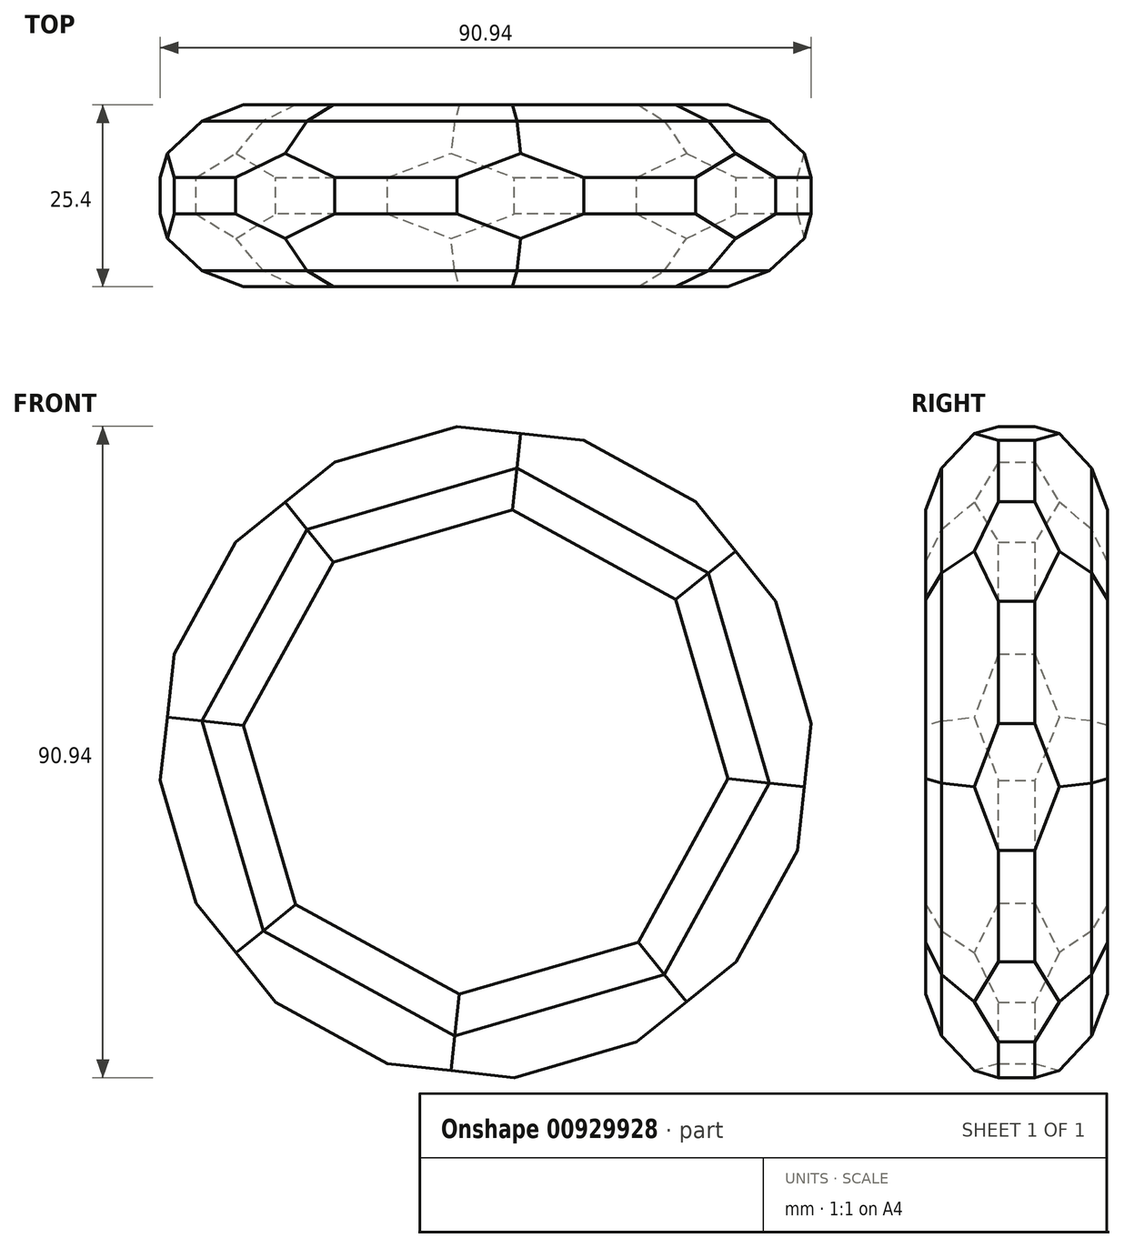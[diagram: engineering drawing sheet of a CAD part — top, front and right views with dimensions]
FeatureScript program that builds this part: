
annotation { "Feature Type Name" : "Feature", "Feature Type Description" : "" }
export const myFeature = defineFeature(function(context is Context, id is Id, definition is map)
    precondition{}
    {
        {
            var Q0;
            Q0=qCreatedBy(makeId("Front.planeOp"),FACE);
            var sketch = newSketch(context, id + "F0", { "sketchPlane" : qUnion([Q0])});
            skCircle(sketch, "E0.cCircle", {"center": v(0, 0) * mm, "radius": 44.76 * mm, "construction": true});
            skLineSegment(sketch, "E0.0", {"start": v(29.33, 34.97) * mm, "end": v(40.48, 21.08) * mm});
            skLineSegment(sketch, "E0.1", {"start": v(40.48, 21.08) * mm, "end": v(45.47, 3.99) * mm});
            skLineSegment(sketch, "E0.2", {"start": v(45.47, 3.99) * mm, "end": v(43.53, -13.72) * mm});
            skLineSegment(sketch, "E0.3", {"start": v(43.53, -13.72) * mm, "end": v(34.97, -29.33) * mm});
            skLineSegment(sketch, "E0.4", {"start": v(34.97, -29.33) * mm, "end": v(21.08, -40.48) * mm});
            skLineSegment(sketch, "E0.5", {"start": v(21.08, -40.48) * mm, "end": v(3.99, -45.47) * mm});
            skLineSegment(sketch, "E0.6", {"start": v(3.99, -45.47) * mm, "end": v(-13.72, -43.53) * mm});
            skLineSegment(sketch, "E0.7", {"start": v(-13.72, -43.53) * mm, "end": v(-29.33, -34.97) * mm});
            skLineSegment(sketch, "E0.8", {"start": v(-29.33, -34.97) * mm, "end": v(-40.48, -21.08) * mm});
            skLineSegment(sketch, "E0.9", {"start": v(-40.48, -21.08) * mm, "end": v(-45.47, -3.99) * mm});
            skLineSegment(sketch, "E0.10", {"start": v(-45.47, -3.99) * mm, "end": v(-43.53, 13.72) * mm});
            skLineSegment(sketch, "E0.11", {"start": v(-43.53, 13.72) * mm, "end": v(-34.97, 29.33) * mm});
            skLineSegment(sketch, "E0.12", {"start": v(-34.97, 29.33) * mm, "end": v(-21.08, 40.48) * mm});
            skLineSegment(sketch, "E0.13", {"start": v(-21.08, 40.48) * mm, "end": v(-3.99, 45.47) * mm});
            skLineSegment(sketch, "E0.14", {"start": v(-3.99, 45.47) * mm, "end": v(13.72, 43.53) * mm});
            skLineSegment(sketch, "E0.15", {"start": v(13.72, 43.53) * mm, "end": v(29.33, 34.97) * mm});
            skPoint(sketch, "E0.0.midPoint", {"position": v(34.9, 28.03) * mm});
            skSolve(sketch);
        }
        {
            var Q0;
            Q0 = qSketchRegion(id + "F0", true);
            extrude(context, id + "F1", {"entities" : qUnion([Q0]), "depth" : 25.4 * mm, "offsetDistance" : 25.4 * mm});
        }
        {
            var Q0;
            Q0=makeQuery(id+"F1.opExtrude","CAP_EDGE",EDGE,{"disambiguationData":[OSD([sQuery(id+"F0.wireOp",EDGE,"E0.3")])],"isStart":false});
            var Q1;
            Q1=makeQuery(id+"F1.opExtrude","CAP_EDGE",EDGE,{"disambiguationData":[OSD([sQuery(id+"F0.wireOp",EDGE,"E0.1")])],"isStart":false});
            var Q2;
            Q2=makeQuery(id+"F1.opExtrude","CAP_EDGE",EDGE,{"disambiguationData":[OSD([sQuery(id+"F0.wireOp",EDGE,"E0.15")])],"isStart":false});
            var Q3;
            Q3=makeQuery(id+"F1.opExtrude","CAP_EDGE",EDGE,{"disambiguationData":[OSD([sQuery(id+"F0.wireOp",EDGE,"E0.13")])],"isStart":false});
            var Q4;
            Q4=makeQuery(id+"F1.opExtrude","CAP_EDGE",EDGE,{"disambiguationData":[OSD([sQuery(id+"F0.wireOp",EDGE,"E0.11")])],"isStart":false});
            var Q5;
            Q5=makeQuery(id+"F1.opExtrude","CAP_EDGE",EDGE,{"disambiguationData":[OSD([sQuery(id+"F0.wireOp",EDGE,"E0.9")])],"isStart":false});
            var Q6;
            Q6=makeQuery(id+"F1.opExtrude","CAP_EDGE",EDGE,{"disambiguationData":[OSD([sQuery(id+"F0.wireOp",EDGE,"E0.7")])],"isStart":false});
            var Q7;
            Q7=makeQuery(id+"F1.opExtrude","CAP_EDGE",EDGE,{"disambiguationData":[OSD([sQuery(id+"F0.wireOp",EDGE,"E0.5")])],"isStart":false});
            chamfer(context, id + "F2", {"entities" : qUnion([Q0, Q1, Q2, Q3, Q4, Q5, Q6, Q7]), "width" : 10.16 * mm, "tangentPropagation" : true});
        }
        {
            var Q0;
            {var subQ0=sQuery(id+"F0.wireOp",EDGE,"E0.11");Q0=makeQuery(id+"F2.opChamfer","BLEND_EDGE",EDGE,{"blendedFrom":[makeQuery(id+"F1.opExtrude","CAP_EDGE",EDGE,{"disambiguationData":[OSD([subQ0])],"isStart":false}),makeQuery(id+"F1.opExtrude","CAP_FACE",FACE,{"disambiguationData":[OSD([sQuery(id+"F0.wireOp",EDGE,"E0.0"),sQuery(id+"F0.wireOp",EDGE,"E0.1"),sQuery(id+"F0.wireOp",EDGE,"E0.2"),sQuery(id+"F0.wireOp",EDGE,"E0.3"),sQuery(id+"F0.wireOp",EDGE,"E0.4"),sQuery(id+"F0.wireOp",EDGE,"E0.5"),sQuery(id+"F0.wireOp",EDGE,"E0.6"),sQuery(id+"F0.wireOp",EDGE,"E0.7"),sQuery(id+"F0.wireOp",EDGE,"E0.8"),sQuery(id+"F0.wireOp",EDGE,"E0.9"),sQuery(id+"F0.wireOp",EDGE,"E0.10"),subQ0,sQuery(id+"F0.wireOp",EDGE,"E0.12"),sQuery(id+"F0.wireOp",EDGE,"E0.13"),sQuery(id+"F0.wireOp",EDGE,"E0.14"),sQuery(id+"F0.wireOp",EDGE,"E0.15")])],"isStart":false})],"blendedInto":[makeQuery(id+"F1.opExtrude","CAP_FACE",FACE,{"disambiguationData":[OSD([sQuery(id+"F0.wireOp",EDGE,"E0.0"),sQuery(id+"F0.wireOp",EDGE,"E0.1"),sQuery(id+"F0.wireOp",EDGE,"E0.2"),sQuery(id+"F0.wireOp",EDGE,"E0.3"),sQuery(id+"F0.wireOp",EDGE,"E0.4"),sQuery(id+"F0.wireOp",EDGE,"E0.5"),sQuery(id+"F0.wireOp",EDGE,"E0.6"),sQuery(id+"F0.wireOp",EDGE,"E0.7"),sQuery(id+"F0.wireOp",EDGE,"E0.8"),sQuery(id+"F0.wireOp",EDGE,"E0.9"),sQuery(id+"F0.wireOp",EDGE,"E0.10"),subQ0,sQuery(id+"F0.wireOp",EDGE,"E0.12"),sQuery(id+"F0.wireOp",EDGE,"E0.13"),sQuery(id+"F0.wireOp",EDGE,"E0.14"),sQuery(id+"F0.wireOp",EDGE,"E0.15")])],"isStart":false})]});}
            var Q1;
            {var subQ0=sQuery(id+"F0.wireOp",EDGE,"E0.15");Q1=makeQuery(id+"F2.opChamfer","BLEND_EDGE",EDGE,{"blendedFrom":[makeQuery(id+"F1.opExtrude","CAP_EDGE",EDGE,{"disambiguationData":[OSD([subQ0])],"isStart":false}),makeQuery(id+"F1.opExtrude","CAP_FACE",FACE,{"disambiguationData":[OSD([sQuery(id+"F0.wireOp",EDGE,"E0.0"),sQuery(id+"F0.wireOp",EDGE,"E0.1"),sQuery(id+"F0.wireOp",EDGE,"E0.2"),sQuery(id+"F0.wireOp",EDGE,"E0.3"),sQuery(id+"F0.wireOp",EDGE,"E0.4"),sQuery(id+"F0.wireOp",EDGE,"E0.5"),sQuery(id+"F0.wireOp",EDGE,"E0.6"),sQuery(id+"F0.wireOp",EDGE,"E0.7"),sQuery(id+"F0.wireOp",EDGE,"E0.8"),sQuery(id+"F0.wireOp",EDGE,"E0.9"),sQuery(id+"F0.wireOp",EDGE,"E0.10"),sQuery(id+"F0.wireOp",EDGE,"E0.11"),sQuery(id+"F0.wireOp",EDGE,"E0.12"),sQuery(id+"F0.wireOp",EDGE,"E0.13"),sQuery(id+"F0.wireOp",EDGE,"E0.14"),subQ0])],"isStart":false})],"blendedInto":[makeQuery(id+"F1.opExtrude","CAP_FACE",FACE,{"disambiguationData":[OSD([sQuery(id+"F0.wireOp",EDGE,"E0.0"),sQuery(id+"F0.wireOp",EDGE,"E0.1"),sQuery(id+"F0.wireOp",EDGE,"E0.2"),sQuery(id+"F0.wireOp",EDGE,"E0.3"),sQuery(id+"F0.wireOp",EDGE,"E0.4"),sQuery(id+"F0.wireOp",EDGE,"E0.5"),sQuery(id+"F0.wireOp",EDGE,"E0.6"),sQuery(id+"F0.wireOp",EDGE,"E0.7"),sQuery(id+"F0.wireOp",EDGE,"E0.8"),sQuery(id+"F0.wireOp",EDGE,"E0.9"),sQuery(id+"F0.wireOp",EDGE,"E0.10"),sQuery(id+"F0.wireOp",EDGE,"E0.11"),sQuery(id+"F0.wireOp",EDGE,"E0.12"),sQuery(id+"F0.wireOp",EDGE,"E0.13"),sQuery(id+"F0.wireOp",EDGE,"E0.14"),subQ0])],"isStart":false})]});}
            var Q2;
            {var subQ0=sQuery(id+"F0.wireOp",EDGE,"E0.3");Q2=makeQuery(id+"F2.opChamfer","BLEND_EDGE",EDGE,{"blendedFrom":[makeQuery(id+"F1.opExtrude","CAP_EDGE",EDGE,{"disambiguationData":[OSD([subQ0])],"isStart":false}),makeQuery(id+"F1.opExtrude","CAP_FACE",FACE,{"disambiguationData":[OSD([sQuery(id+"F0.wireOp",EDGE,"E0.0"),sQuery(id+"F0.wireOp",EDGE,"E0.1"),sQuery(id+"F0.wireOp",EDGE,"E0.2"),subQ0,sQuery(id+"F0.wireOp",EDGE,"E0.4"),sQuery(id+"F0.wireOp",EDGE,"E0.5"),sQuery(id+"F0.wireOp",EDGE,"E0.6"),sQuery(id+"F0.wireOp",EDGE,"E0.7"),sQuery(id+"F0.wireOp",EDGE,"E0.8"),sQuery(id+"F0.wireOp",EDGE,"E0.9"),sQuery(id+"F0.wireOp",EDGE,"E0.10"),sQuery(id+"F0.wireOp",EDGE,"E0.11"),sQuery(id+"F0.wireOp",EDGE,"E0.12"),sQuery(id+"F0.wireOp",EDGE,"E0.13"),sQuery(id+"F0.wireOp",EDGE,"E0.14"),sQuery(id+"F0.wireOp",EDGE,"E0.15")])],"isStart":false})],"blendedInto":[makeQuery(id+"F1.opExtrude","CAP_FACE",FACE,{"disambiguationData":[OSD([sQuery(id+"F0.wireOp",EDGE,"E0.0"),sQuery(id+"F0.wireOp",EDGE,"E0.1"),sQuery(id+"F0.wireOp",EDGE,"E0.2"),subQ0,sQuery(id+"F0.wireOp",EDGE,"E0.4"),sQuery(id+"F0.wireOp",EDGE,"E0.5"),sQuery(id+"F0.wireOp",EDGE,"E0.6"),sQuery(id+"F0.wireOp",EDGE,"E0.7"),sQuery(id+"F0.wireOp",EDGE,"E0.8"),sQuery(id+"F0.wireOp",EDGE,"E0.9"),sQuery(id+"F0.wireOp",EDGE,"E0.10"),sQuery(id+"F0.wireOp",EDGE,"E0.11"),sQuery(id+"F0.wireOp",EDGE,"E0.12"),sQuery(id+"F0.wireOp",EDGE,"E0.13"),sQuery(id+"F0.wireOp",EDGE,"E0.14"),sQuery(id+"F0.wireOp",EDGE,"E0.15")])],"isStart":false})]});}
            var Q3;
            {var subQ0=sQuery(id+"F0.wireOp",EDGE,"E0.7");Q3=makeQuery(id+"F2.opChamfer","BLEND_EDGE",EDGE,{"blendedFrom":[makeQuery(id+"F1.opExtrude","CAP_EDGE",EDGE,{"disambiguationData":[OSD([subQ0])],"isStart":false}),makeQuery(id+"F1.opExtrude","CAP_FACE",FACE,{"disambiguationData":[OSD([sQuery(id+"F0.wireOp",EDGE,"E0.0"),sQuery(id+"F0.wireOp",EDGE,"E0.1"),sQuery(id+"F0.wireOp",EDGE,"E0.2"),sQuery(id+"F0.wireOp",EDGE,"E0.3"),sQuery(id+"F0.wireOp",EDGE,"E0.4"),sQuery(id+"F0.wireOp",EDGE,"E0.5"),sQuery(id+"F0.wireOp",EDGE,"E0.6"),subQ0,sQuery(id+"F0.wireOp",EDGE,"E0.8"),sQuery(id+"F0.wireOp",EDGE,"E0.9"),sQuery(id+"F0.wireOp",EDGE,"E0.10"),sQuery(id+"F0.wireOp",EDGE,"E0.11"),sQuery(id+"F0.wireOp",EDGE,"E0.12"),sQuery(id+"F0.wireOp",EDGE,"E0.13"),sQuery(id+"F0.wireOp",EDGE,"E0.14"),sQuery(id+"F0.wireOp",EDGE,"E0.15")])],"isStart":false})],"blendedInto":[makeQuery(id+"F1.opExtrude","CAP_FACE",FACE,{"disambiguationData":[OSD([sQuery(id+"F0.wireOp",EDGE,"E0.0"),sQuery(id+"F0.wireOp",EDGE,"E0.1"),sQuery(id+"F0.wireOp",EDGE,"E0.2"),sQuery(id+"F0.wireOp",EDGE,"E0.3"),sQuery(id+"F0.wireOp",EDGE,"E0.4"),sQuery(id+"F0.wireOp",EDGE,"E0.5"),sQuery(id+"F0.wireOp",EDGE,"E0.6"),subQ0,sQuery(id+"F0.wireOp",EDGE,"E0.8"),sQuery(id+"F0.wireOp",EDGE,"E0.9"),sQuery(id+"F0.wireOp",EDGE,"E0.10"),sQuery(id+"F0.wireOp",EDGE,"E0.11"),sQuery(id+"F0.wireOp",EDGE,"E0.12"),sQuery(id+"F0.wireOp",EDGE,"E0.13"),sQuery(id+"F0.wireOp",EDGE,"E0.14"),sQuery(id+"F0.wireOp",EDGE,"E0.15")])],"isStart":false})]});}
            chamfer(context, id + "F3", {"entities" : qUnion([Q0, Q1, Q2, Q3]), "width" : 7.62 * mm, "tangentPropagation" : true});
        }
        {
            var Q0;
            {var subQ0=sQuery(id+"F0.wireOp",EDGE,"E0.13");Q0=makeQuery(id+"F2.opChamfer","BLEND_EDGE",EDGE,{"blendedFrom":[makeQuery(id+"F1.opExtrude","CAP_EDGE",EDGE,{"disambiguationData":[OSD([subQ0])],"isStart":false}),makeQuery(id+"F1.opExtrude","CAP_FACE",FACE,{"disambiguationData":[OSD([sQuery(id+"F0.wireOp",EDGE,"E0.0"),sQuery(id+"F0.wireOp",EDGE,"E0.1"),sQuery(id+"F0.wireOp",EDGE,"E0.2"),sQuery(id+"F0.wireOp",EDGE,"E0.3"),sQuery(id+"F0.wireOp",EDGE,"E0.4"),sQuery(id+"F0.wireOp",EDGE,"E0.5"),sQuery(id+"F0.wireOp",EDGE,"E0.6"),sQuery(id+"F0.wireOp",EDGE,"E0.7"),sQuery(id+"F0.wireOp",EDGE,"E0.8"),sQuery(id+"F0.wireOp",EDGE,"E0.9"),sQuery(id+"F0.wireOp",EDGE,"E0.10"),sQuery(id+"F0.wireOp",EDGE,"E0.11"),sQuery(id+"F0.wireOp",EDGE,"E0.12"),subQ0,sQuery(id+"F0.wireOp",EDGE,"E0.14"),sQuery(id+"F0.wireOp",EDGE,"E0.15")])],"isStart":false})],"blendedInto":[makeQuery(id+"F1.opExtrude","CAP_FACE",FACE,{"disambiguationData":[OSD([sQuery(id+"F0.wireOp",EDGE,"E0.0"),sQuery(id+"F0.wireOp",EDGE,"E0.1"),sQuery(id+"F0.wireOp",EDGE,"E0.2"),sQuery(id+"F0.wireOp",EDGE,"E0.3"),sQuery(id+"F0.wireOp",EDGE,"E0.4"),sQuery(id+"F0.wireOp",EDGE,"E0.5"),sQuery(id+"F0.wireOp",EDGE,"E0.6"),sQuery(id+"F0.wireOp",EDGE,"E0.7"),sQuery(id+"F0.wireOp",EDGE,"E0.8"),sQuery(id+"F0.wireOp",EDGE,"E0.9"),sQuery(id+"F0.wireOp",EDGE,"E0.10"),sQuery(id+"F0.wireOp",EDGE,"E0.11"),sQuery(id+"F0.wireOp",EDGE,"E0.12"),subQ0,sQuery(id+"F0.wireOp",EDGE,"E0.14"),sQuery(id+"F0.wireOp",EDGE,"E0.15")])],"isStart":false})]});}
            var Q1;
            {var subQ0=sQuery(id+"F0.wireOp",EDGE,"E0.1");Q1=makeQuery(id+"F2.opChamfer","BLEND_EDGE",EDGE,{"blendedFrom":[makeQuery(id+"F1.opExtrude","CAP_EDGE",EDGE,{"disambiguationData":[OSD([subQ0])],"isStart":false}),makeQuery(id+"F1.opExtrude","CAP_FACE",FACE,{"disambiguationData":[OSD([sQuery(id+"F0.wireOp",EDGE,"E0.0"),subQ0,sQuery(id+"F0.wireOp",EDGE,"E0.2"),sQuery(id+"F0.wireOp",EDGE,"E0.3"),sQuery(id+"F0.wireOp",EDGE,"E0.4"),sQuery(id+"F0.wireOp",EDGE,"E0.5"),sQuery(id+"F0.wireOp",EDGE,"E0.6"),sQuery(id+"F0.wireOp",EDGE,"E0.7"),sQuery(id+"F0.wireOp",EDGE,"E0.8"),sQuery(id+"F0.wireOp",EDGE,"E0.9"),sQuery(id+"F0.wireOp",EDGE,"E0.10"),sQuery(id+"F0.wireOp",EDGE,"E0.11"),sQuery(id+"F0.wireOp",EDGE,"E0.12"),sQuery(id+"F0.wireOp",EDGE,"E0.13"),sQuery(id+"F0.wireOp",EDGE,"E0.14"),sQuery(id+"F0.wireOp",EDGE,"E0.15")])],"isStart":false})],"blendedInto":[makeQuery(id+"F1.opExtrude","CAP_FACE",FACE,{"disambiguationData":[OSD([sQuery(id+"F0.wireOp",EDGE,"E0.0"),subQ0,sQuery(id+"F0.wireOp",EDGE,"E0.2"),sQuery(id+"F0.wireOp",EDGE,"E0.3"),sQuery(id+"F0.wireOp",EDGE,"E0.4"),sQuery(id+"F0.wireOp",EDGE,"E0.5"),sQuery(id+"F0.wireOp",EDGE,"E0.6"),sQuery(id+"F0.wireOp",EDGE,"E0.7"),sQuery(id+"F0.wireOp",EDGE,"E0.8"),sQuery(id+"F0.wireOp",EDGE,"E0.9"),sQuery(id+"F0.wireOp",EDGE,"E0.10"),sQuery(id+"F0.wireOp",EDGE,"E0.11"),sQuery(id+"F0.wireOp",EDGE,"E0.12"),sQuery(id+"F0.wireOp",EDGE,"E0.13"),sQuery(id+"F0.wireOp",EDGE,"E0.14"),sQuery(id+"F0.wireOp",EDGE,"E0.15")])],"isStart":false})]});}
            var Q2;
            {var subQ0=sQuery(id+"F0.wireOp",EDGE,"E0.5");Q2=makeQuery(id+"F2.opChamfer","BLEND_EDGE",EDGE,{"blendedFrom":[makeQuery(id+"F1.opExtrude","CAP_EDGE",EDGE,{"disambiguationData":[OSD([subQ0])],"isStart":false}),makeQuery(id+"F1.opExtrude","CAP_FACE",FACE,{"disambiguationData":[OSD([sQuery(id+"F0.wireOp",EDGE,"E0.0"),sQuery(id+"F0.wireOp",EDGE,"E0.1"),sQuery(id+"F0.wireOp",EDGE,"E0.2"),sQuery(id+"F0.wireOp",EDGE,"E0.3"),sQuery(id+"F0.wireOp",EDGE,"E0.4"),subQ0,sQuery(id+"F0.wireOp",EDGE,"E0.6"),sQuery(id+"F0.wireOp",EDGE,"E0.7"),sQuery(id+"F0.wireOp",EDGE,"E0.8"),sQuery(id+"F0.wireOp",EDGE,"E0.9"),sQuery(id+"F0.wireOp",EDGE,"E0.10"),sQuery(id+"F0.wireOp",EDGE,"E0.11"),sQuery(id+"F0.wireOp",EDGE,"E0.12"),sQuery(id+"F0.wireOp",EDGE,"E0.13"),sQuery(id+"F0.wireOp",EDGE,"E0.14"),sQuery(id+"F0.wireOp",EDGE,"E0.15")])],"isStart":false})],"blendedInto":[makeQuery(id+"F1.opExtrude","CAP_FACE",FACE,{"disambiguationData":[OSD([sQuery(id+"F0.wireOp",EDGE,"E0.0"),sQuery(id+"F0.wireOp",EDGE,"E0.1"),sQuery(id+"F0.wireOp",EDGE,"E0.2"),sQuery(id+"F0.wireOp",EDGE,"E0.3"),sQuery(id+"F0.wireOp",EDGE,"E0.4"),subQ0,sQuery(id+"F0.wireOp",EDGE,"E0.6"),sQuery(id+"F0.wireOp",EDGE,"E0.7"),sQuery(id+"F0.wireOp",EDGE,"E0.8"),sQuery(id+"F0.wireOp",EDGE,"E0.9"),sQuery(id+"F0.wireOp",EDGE,"E0.10"),sQuery(id+"F0.wireOp",EDGE,"E0.11"),sQuery(id+"F0.wireOp",EDGE,"E0.12"),sQuery(id+"F0.wireOp",EDGE,"E0.13"),sQuery(id+"F0.wireOp",EDGE,"E0.14"),sQuery(id+"F0.wireOp",EDGE,"E0.15")])],"isStart":false})]});}
            var Q3;
            {var subQ0=sQuery(id+"F0.wireOp",EDGE,"E0.9");Q3=makeQuery(id+"F2.opChamfer","BLEND_EDGE",EDGE,{"blendedFrom":[makeQuery(id+"F1.opExtrude","CAP_EDGE",EDGE,{"disambiguationData":[OSD([subQ0])],"isStart":false}),makeQuery(id+"F1.opExtrude","CAP_FACE",FACE,{"disambiguationData":[OSD([sQuery(id+"F0.wireOp",EDGE,"E0.0"),sQuery(id+"F0.wireOp",EDGE,"E0.1"),sQuery(id+"F0.wireOp",EDGE,"E0.2"),sQuery(id+"F0.wireOp",EDGE,"E0.3"),sQuery(id+"F0.wireOp",EDGE,"E0.4"),sQuery(id+"F0.wireOp",EDGE,"E0.5"),sQuery(id+"F0.wireOp",EDGE,"E0.6"),sQuery(id+"F0.wireOp",EDGE,"E0.7"),sQuery(id+"F0.wireOp",EDGE,"E0.8"),subQ0,sQuery(id+"F0.wireOp",EDGE,"E0.10"),sQuery(id+"F0.wireOp",EDGE,"E0.11"),sQuery(id+"F0.wireOp",EDGE,"E0.12"),sQuery(id+"F0.wireOp",EDGE,"E0.13"),sQuery(id+"F0.wireOp",EDGE,"E0.14"),sQuery(id+"F0.wireOp",EDGE,"E0.15")])],"isStart":false})],"blendedInto":[makeQuery(id+"F1.opExtrude","CAP_FACE",FACE,{"disambiguationData":[OSD([sQuery(id+"F0.wireOp",EDGE,"E0.0"),sQuery(id+"F0.wireOp",EDGE,"E0.1"),sQuery(id+"F0.wireOp",EDGE,"E0.2"),sQuery(id+"F0.wireOp",EDGE,"E0.3"),sQuery(id+"F0.wireOp",EDGE,"E0.4"),sQuery(id+"F0.wireOp",EDGE,"E0.5"),sQuery(id+"F0.wireOp",EDGE,"E0.6"),sQuery(id+"F0.wireOp",EDGE,"E0.7"),sQuery(id+"F0.wireOp",EDGE,"E0.8"),subQ0,sQuery(id+"F0.wireOp",EDGE,"E0.10"),sQuery(id+"F0.wireOp",EDGE,"E0.11"),sQuery(id+"F0.wireOp",EDGE,"E0.12"),sQuery(id+"F0.wireOp",EDGE,"E0.13"),sQuery(id+"F0.wireOp",EDGE,"E0.14"),sQuery(id+"F0.wireOp",EDGE,"E0.15")])],"isStart":false})]});}
            chamfer(context, id + "F4", {"entities" : qUnion([Q0, Q1, Q2, Q3]), "width" : 7.62 * mm, "tangentPropagation" : true});
        }
        {
            var Q0;
            Q0=makeQuery(id+"F1.opExtrude","CAP_EDGE",EDGE,{"disambiguationData":[OSD([sQuery(id+"F0.wireOp",EDGE,"E0.7")])],"isStart":true});
            var Q1;
            Q1=makeQuery(id+"F1.opExtrude","CAP_EDGE",EDGE,{"disambiguationData":[OSD([sQuery(id+"F0.wireOp",EDGE,"E0.5")])],"isStart":true});
            var Q2;
            Q2=makeQuery(id+"F1.opExtrude","CAP_EDGE",EDGE,{"disambiguationData":[OSD([sQuery(id+"F0.wireOp",EDGE,"E0.3")])],"isStart":true});
            var Q3;
            Q3=makeQuery(id+"F1.opExtrude","CAP_EDGE",EDGE,{"disambiguationData":[OSD([sQuery(id+"F0.wireOp",EDGE,"E0.1")])],"isStart":true});
            var Q4;
            Q4=makeQuery(id+"F1.opExtrude","CAP_EDGE",EDGE,{"disambiguationData":[OSD([sQuery(id+"F0.wireOp",EDGE,"E0.15")])],"isStart":true});
            var Q5;
            Q5=makeQuery(id+"F1.opExtrude","CAP_EDGE",EDGE,{"disambiguationData":[OSD([sQuery(id+"F0.wireOp",EDGE,"E0.13")])],"isStart":true});
            var Q6;
            Q6=makeQuery(id+"F1.opExtrude","CAP_EDGE",EDGE,{"disambiguationData":[OSD([sQuery(id+"F0.wireOp",EDGE,"E0.11")])],"isStart":true});
            var Q7;
            Q7=makeQuery(id+"F1.opExtrude","CAP_EDGE",EDGE,{"disambiguationData":[OSD([sQuery(id+"F0.wireOp",EDGE,"E0.9")])],"isStart":true});
            chamfer(context, id + "F5", {"entities" : qUnion([Q0, Q1, Q2, Q3, Q4, Q5, Q6, Q7]), "width" : 10.16 * mm, "tangentPropagation" : true});
        }
        {
            var Q0;
            {var subQ0=sQuery(id+"F0.wireOp",EDGE,"E0.15");Q0=makeQuery(id+"F5.opChamfer","BLEND_EDGE",EDGE,{"blendedFrom":[makeQuery(id+"F1.opExtrude","CAP_EDGE",EDGE,{"disambiguationData":[OSD([subQ0])],"isStart":true}),makeQuery(id+"F1.opExtrude","CAP_FACE",FACE,{"disambiguationData":[OSD([sQuery(id+"F0.wireOp",EDGE,"E0.0"),sQuery(id+"F0.wireOp",EDGE,"E0.1"),sQuery(id+"F0.wireOp",EDGE,"E0.2"),sQuery(id+"F0.wireOp",EDGE,"E0.3"),sQuery(id+"F0.wireOp",EDGE,"E0.4"),sQuery(id+"F0.wireOp",EDGE,"E0.5"),sQuery(id+"F0.wireOp",EDGE,"E0.6"),sQuery(id+"F0.wireOp",EDGE,"E0.7"),sQuery(id+"F0.wireOp",EDGE,"E0.8"),sQuery(id+"F0.wireOp",EDGE,"E0.9"),sQuery(id+"F0.wireOp",EDGE,"E0.10"),sQuery(id+"F0.wireOp",EDGE,"E0.11"),sQuery(id+"F0.wireOp",EDGE,"E0.12"),sQuery(id+"F0.wireOp",EDGE,"E0.13"),sQuery(id+"F0.wireOp",EDGE,"E0.14"),subQ0])],"isStart":true})],"blendedInto":[makeQuery(id+"F1.opExtrude","CAP_FACE",FACE,{"disambiguationData":[OSD([sQuery(id+"F0.wireOp",EDGE,"E0.0"),sQuery(id+"F0.wireOp",EDGE,"E0.1"),sQuery(id+"F0.wireOp",EDGE,"E0.2"),sQuery(id+"F0.wireOp",EDGE,"E0.3"),sQuery(id+"F0.wireOp",EDGE,"E0.4"),sQuery(id+"F0.wireOp",EDGE,"E0.5"),sQuery(id+"F0.wireOp",EDGE,"E0.6"),sQuery(id+"F0.wireOp",EDGE,"E0.7"),sQuery(id+"F0.wireOp",EDGE,"E0.8"),sQuery(id+"F0.wireOp",EDGE,"E0.9"),sQuery(id+"F0.wireOp",EDGE,"E0.10"),sQuery(id+"F0.wireOp",EDGE,"E0.11"),sQuery(id+"F0.wireOp",EDGE,"E0.12"),sQuery(id+"F0.wireOp",EDGE,"E0.13"),sQuery(id+"F0.wireOp",EDGE,"E0.14"),subQ0])],"isStart":true})]});}
            var Q1;
            {var subQ0=sQuery(id+"F0.wireOp",EDGE,"E0.13");Q1=makeQuery(id+"F5.opChamfer","BLEND_EDGE",EDGE,{"blendedFrom":[makeQuery(id+"F1.opExtrude","CAP_EDGE",EDGE,{"disambiguationData":[OSD([subQ0])],"isStart":true}),makeQuery(id+"F1.opExtrude","CAP_FACE",FACE,{"disambiguationData":[OSD([sQuery(id+"F0.wireOp",EDGE,"E0.0"),sQuery(id+"F0.wireOp",EDGE,"E0.1"),sQuery(id+"F0.wireOp",EDGE,"E0.2"),sQuery(id+"F0.wireOp",EDGE,"E0.3"),sQuery(id+"F0.wireOp",EDGE,"E0.4"),sQuery(id+"F0.wireOp",EDGE,"E0.5"),sQuery(id+"F0.wireOp",EDGE,"E0.6"),sQuery(id+"F0.wireOp",EDGE,"E0.7"),sQuery(id+"F0.wireOp",EDGE,"E0.8"),sQuery(id+"F0.wireOp",EDGE,"E0.9"),sQuery(id+"F0.wireOp",EDGE,"E0.10"),sQuery(id+"F0.wireOp",EDGE,"E0.11"),sQuery(id+"F0.wireOp",EDGE,"E0.12"),subQ0,sQuery(id+"F0.wireOp",EDGE,"E0.14"),sQuery(id+"F0.wireOp",EDGE,"E0.15")])],"isStart":true})],"blendedInto":[makeQuery(id+"F1.opExtrude","CAP_FACE",FACE,{"disambiguationData":[OSD([sQuery(id+"F0.wireOp",EDGE,"E0.0"),sQuery(id+"F0.wireOp",EDGE,"E0.1"),sQuery(id+"F0.wireOp",EDGE,"E0.2"),sQuery(id+"F0.wireOp",EDGE,"E0.3"),sQuery(id+"F0.wireOp",EDGE,"E0.4"),sQuery(id+"F0.wireOp",EDGE,"E0.5"),sQuery(id+"F0.wireOp",EDGE,"E0.6"),sQuery(id+"F0.wireOp",EDGE,"E0.7"),sQuery(id+"F0.wireOp",EDGE,"E0.8"),sQuery(id+"F0.wireOp",EDGE,"E0.9"),sQuery(id+"F0.wireOp",EDGE,"E0.10"),sQuery(id+"F0.wireOp",EDGE,"E0.11"),sQuery(id+"F0.wireOp",EDGE,"E0.12"),subQ0,sQuery(id+"F0.wireOp",EDGE,"E0.14"),sQuery(id+"F0.wireOp",EDGE,"E0.15")])],"isStart":true})]});}
            var Q2;
            {var subQ0=sQuery(id+"F0.wireOp",EDGE,"E0.11");Q2=makeQuery(id+"F5.opChamfer","BLEND_EDGE",EDGE,{"blendedFrom":[makeQuery(id+"F1.opExtrude","CAP_EDGE",EDGE,{"disambiguationData":[OSD([subQ0])],"isStart":true}),makeQuery(id+"F1.opExtrude","CAP_FACE",FACE,{"disambiguationData":[OSD([sQuery(id+"F0.wireOp",EDGE,"E0.0"),sQuery(id+"F0.wireOp",EDGE,"E0.1"),sQuery(id+"F0.wireOp",EDGE,"E0.2"),sQuery(id+"F0.wireOp",EDGE,"E0.3"),sQuery(id+"F0.wireOp",EDGE,"E0.4"),sQuery(id+"F0.wireOp",EDGE,"E0.5"),sQuery(id+"F0.wireOp",EDGE,"E0.6"),sQuery(id+"F0.wireOp",EDGE,"E0.7"),sQuery(id+"F0.wireOp",EDGE,"E0.8"),sQuery(id+"F0.wireOp",EDGE,"E0.9"),sQuery(id+"F0.wireOp",EDGE,"E0.10"),subQ0,sQuery(id+"F0.wireOp",EDGE,"E0.12"),sQuery(id+"F0.wireOp",EDGE,"E0.13"),sQuery(id+"F0.wireOp",EDGE,"E0.14"),sQuery(id+"F0.wireOp",EDGE,"E0.15")])],"isStart":true})],"blendedInto":[makeQuery(id+"F1.opExtrude","CAP_FACE",FACE,{"disambiguationData":[OSD([sQuery(id+"F0.wireOp",EDGE,"E0.0"),sQuery(id+"F0.wireOp",EDGE,"E0.1"),sQuery(id+"F0.wireOp",EDGE,"E0.2"),sQuery(id+"F0.wireOp",EDGE,"E0.3"),sQuery(id+"F0.wireOp",EDGE,"E0.4"),sQuery(id+"F0.wireOp",EDGE,"E0.5"),sQuery(id+"F0.wireOp",EDGE,"E0.6"),sQuery(id+"F0.wireOp",EDGE,"E0.7"),sQuery(id+"F0.wireOp",EDGE,"E0.8"),sQuery(id+"F0.wireOp",EDGE,"E0.9"),sQuery(id+"F0.wireOp",EDGE,"E0.10"),subQ0,sQuery(id+"F0.wireOp",EDGE,"E0.12"),sQuery(id+"F0.wireOp",EDGE,"E0.13"),sQuery(id+"F0.wireOp",EDGE,"E0.14"),sQuery(id+"F0.wireOp",EDGE,"E0.15")])],"isStart":true})]});}
            var Q3;
            {var subQ0=sQuery(id+"F0.wireOp",EDGE,"E0.9");Q3=makeQuery(id+"F5.opChamfer","BLEND_EDGE",EDGE,{"blendedFrom":[makeQuery(id+"F1.opExtrude","CAP_EDGE",EDGE,{"disambiguationData":[OSD([subQ0])],"isStart":true}),makeQuery(id+"F1.opExtrude","CAP_FACE",FACE,{"disambiguationData":[OSD([sQuery(id+"F0.wireOp",EDGE,"E0.0"),sQuery(id+"F0.wireOp",EDGE,"E0.1"),sQuery(id+"F0.wireOp",EDGE,"E0.2"),sQuery(id+"F0.wireOp",EDGE,"E0.3"),sQuery(id+"F0.wireOp",EDGE,"E0.4"),sQuery(id+"F0.wireOp",EDGE,"E0.5"),sQuery(id+"F0.wireOp",EDGE,"E0.6"),sQuery(id+"F0.wireOp",EDGE,"E0.7"),sQuery(id+"F0.wireOp",EDGE,"E0.8"),subQ0,sQuery(id+"F0.wireOp",EDGE,"E0.10"),sQuery(id+"F0.wireOp",EDGE,"E0.11"),sQuery(id+"F0.wireOp",EDGE,"E0.12"),sQuery(id+"F0.wireOp",EDGE,"E0.13"),sQuery(id+"F0.wireOp",EDGE,"E0.14"),sQuery(id+"F0.wireOp",EDGE,"E0.15")])],"isStart":true})],"blendedInto":[makeQuery(id+"F1.opExtrude","CAP_FACE",FACE,{"disambiguationData":[OSD([sQuery(id+"F0.wireOp",EDGE,"E0.0"),sQuery(id+"F0.wireOp",EDGE,"E0.1"),sQuery(id+"F0.wireOp",EDGE,"E0.2"),sQuery(id+"F0.wireOp",EDGE,"E0.3"),sQuery(id+"F0.wireOp",EDGE,"E0.4"),sQuery(id+"F0.wireOp",EDGE,"E0.5"),sQuery(id+"F0.wireOp",EDGE,"E0.6"),sQuery(id+"F0.wireOp",EDGE,"E0.7"),sQuery(id+"F0.wireOp",EDGE,"E0.8"),subQ0,sQuery(id+"F0.wireOp",EDGE,"E0.10"),sQuery(id+"F0.wireOp",EDGE,"E0.11"),sQuery(id+"F0.wireOp",EDGE,"E0.12"),sQuery(id+"F0.wireOp",EDGE,"E0.13"),sQuery(id+"F0.wireOp",EDGE,"E0.14"),sQuery(id+"F0.wireOp",EDGE,"E0.15")])],"isStart":true})]});}
            var Q4;
            {var subQ0=sQuery(id+"F0.wireOp",EDGE,"E0.7");Q4=makeQuery(id+"F5.opChamfer","BLEND_EDGE",EDGE,{"blendedFrom":[makeQuery(id+"F1.opExtrude","CAP_EDGE",EDGE,{"disambiguationData":[OSD([subQ0])],"isStart":true}),makeQuery(id+"F1.opExtrude","CAP_FACE",FACE,{"disambiguationData":[OSD([sQuery(id+"F0.wireOp",EDGE,"E0.0"),sQuery(id+"F0.wireOp",EDGE,"E0.1"),sQuery(id+"F0.wireOp",EDGE,"E0.2"),sQuery(id+"F0.wireOp",EDGE,"E0.3"),sQuery(id+"F0.wireOp",EDGE,"E0.4"),sQuery(id+"F0.wireOp",EDGE,"E0.5"),sQuery(id+"F0.wireOp",EDGE,"E0.6"),subQ0,sQuery(id+"F0.wireOp",EDGE,"E0.8"),sQuery(id+"F0.wireOp",EDGE,"E0.9"),sQuery(id+"F0.wireOp",EDGE,"E0.10"),sQuery(id+"F0.wireOp",EDGE,"E0.11"),sQuery(id+"F0.wireOp",EDGE,"E0.12"),sQuery(id+"F0.wireOp",EDGE,"E0.13"),sQuery(id+"F0.wireOp",EDGE,"E0.14"),sQuery(id+"F0.wireOp",EDGE,"E0.15")])],"isStart":true})],"blendedInto":[makeQuery(id+"F1.opExtrude","CAP_FACE",FACE,{"disambiguationData":[OSD([sQuery(id+"F0.wireOp",EDGE,"E0.0"),sQuery(id+"F0.wireOp",EDGE,"E0.1"),sQuery(id+"F0.wireOp",EDGE,"E0.2"),sQuery(id+"F0.wireOp",EDGE,"E0.3"),sQuery(id+"F0.wireOp",EDGE,"E0.4"),sQuery(id+"F0.wireOp",EDGE,"E0.5"),sQuery(id+"F0.wireOp",EDGE,"E0.6"),subQ0,sQuery(id+"F0.wireOp",EDGE,"E0.8"),sQuery(id+"F0.wireOp",EDGE,"E0.9"),sQuery(id+"F0.wireOp",EDGE,"E0.10"),sQuery(id+"F0.wireOp",EDGE,"E0.11"),sQuery(id+"F0.wireOp",EDGE,"E0.12"),sQuery(id+"F0.wireOp",EDGE,"E0.13"),sQuery(id+"F0.wireOp",EDGE,"E0.14"),sQuery(id+"F0.wireOp",EDGE,"E0.15")])],"isStart":true})]});}
            var Q5;
            {var subQ0=sQuery(id+"F0.wireOp",EDGE,"E0.5");Q5=makeQuery(id+"F5.opChamfer","BLEND_EDGE",EDGE,{"blendedFrom":[makeQuery(id+"F1.opExtrude","CAP_EDGE",EDGE,{"disambiguationData":[OSD([subQ0])],"isStart":true}),makeQuery(id+"F1.opExtrude","CAP_FACE",FACE,{"disambiguationData":[OSD([sQuery(id+"F0.wireOp",EDGE,"E0.0"),sQuery(id+"F0.wireOp",EDGE,"E0.1"),sQuery(id+"F0.wireOp",EDGE,"E0.2"),sQuery(id+"F0.wireOp",EDGE,"E0.3"),sQuery(id+"F0.wireOp",EDGE,"E0.4"),subQ0,sQuery(id+"F0.wireOp",EDGE,"E0.6"),sQuery(id+"F0.wireOp",EDGE,"E0.7"),sQuery(id+"F0.wireOp",EDGE,"E0.8"),sQuery(id+"F0.wireOp",EDGE,"E0.9"),sQuery(id+"F0.wireOp",EDGE,"E0.10"),sQuery(id+"F0.wireOp",EDGE,"E0.11"),sQuery(id+"F0.wireOp",EDGE,"E0.12"),sQuery(id+"F0.wireOp",EDGE,"E0.13"),sQuery(id+"F0.wireOp",EDGE,"E0.14"),sQuery(id+"F0.wireOp",EDGE,"E0.15")])],"isStart":true})],"blendedInto":[makeQuery(id+"F1.opExtrude","CAP_FACE",FACE,{"disambiguationData":[OSD([sQuery(id+"F0.wireOp",EDGE,"E0.0"),sQuery(id+"F0.wireOp",EDGE,"E0.1"),sQuery(id+"F0.wireOp",EDGE,"E0.2"),sQuery(id+"F0.wireOp",EDGE,"E0.3"),sQuery(id+"F0.wireOp",EDGE,"E0.4"),subQ0,sQuery(id+"F0.wireOp",EDGE,"E0.6"),sQuery(id+"F0.wireOp",EDGE,"E0.7"),sQuery(id+"F0.wireOp",EDGE,"E0.8"),sQuery(id+"F0.wireOp",EDGE,"E0.9"),sQuery(id+"F0.wireOp",EDGE,"E0.10"),sQuery(id+"F0.wireOp",EDGE,"E0.11"),sQuery(id+"F0.wireOp",EDGE,"E0.12"),sQuery(id+"F0.wireOp",EDGE,"E0.13"),sQuery(id+"F0.wireOp",EDGE,"E0.14"),sQuery(id+"F0.wireOp",EDGE,"E0.15")])],"isStart":true})]});}
            var Q6;
            {var subQ0=sQuery(id+"F0.wireOp",EDGE,"E0.3");Q6=makeQuery(id+"F5.opChamfer","BLEND_EDGE",EDGE,{"blendedFrom":[makeQuery(id+"F1.opExtrude","CAP_EDGE",EDGE,{"disambiguationData":[OSD([subQ0])],"isStart":true}),makeQuery(id+"F1.opExtrude","CAP_FACE",FACE,{"disambiguationData":[OSD([sQuery(id+"F0.wireOp",EDGE,"E0.0"),sQuery(id+"F0.wireOp",EDGE,"E0.1"),sQuery(id+"F0.wireOp",EDGE,"E0.2"),subQ0,sQuery(id+"F0.wireOp",EDGE,"E0.4"),sQuery(id+"F0.wireOp",EDGE,"E0.5"),sQuery(id+"F0.wireOp",EDGE,"E0.6"),sQuery(id+"F0.wireOp",EDGE,"E0.7"),sQuery(id+"F0.wireOp",EDGE,"E0.8"),sQuery(id+"F0.wireOp",EDGE,"E0.9"),sQuery(id+"F0.wireOp",EDGE,"E0.10"),sQuery(id+"F0.wireOp",EDGE,"E0.11"),sQuery(id+"F0.wireOp",EDGE,"E0.12"),sQuery(id+"F0.wireOp",EDGE,"E0.13"),sQuery(id+"F0.wireOp",EDGE,"E0.14"),sQuery(id+"F0.wireOp",EDGE,"E0.15")])],"isStart":true})],"blendedInto":[makeQuery(id+"F1.opExtrude","CAP_FACE",FACE,{"disambiguationData":[OSD([sQuery(id+"F0.wireOp",EDGE,"E0.0"),sQuery(id+"F0.wireOp",EDGE,"E0.1"),sQuery(id+"F0.wireOp",EDGE,"E0.2"),subQ0,sQuery(id+"F0.wireOp",EDGE,"E0.4"),sQuery(id+"F0.wireOp",EDGE,"E0.5"),sQuery(id+"F0.wireOp",EDGE,"E0.6"),sQuery(id+"F0.wireOp",EDGE,"E0.7"),sQuery(id+"F0.wireOp",EDGE,"E0.8"),sQuery(id+"F0.wireOp",EDGE,"E0.9"),sQuery(id+"F0.wireOp",EDGE,"E0.10"),sQuery(id+"F0.wireOp",EDGE,"E0.11"),sQuery(id+"F0.wireOp",EDGE,"E0.12"),sQuery(id+"F0.wireOp",EDGE,"E0.13"),sQuery(id+"F0.wireOp",EDGE,"E0.14"),sQuery(id+"F0.wireOp",EDGE,"E0.15")])],"isStart":true})]});}
            var Q7;
            {var subQ0=sQuery(id+"F0.wireOp",EDGE,"E0.1");Q7=makeQuery(id+"F5.opChamfer","BLEND_EDGE",EDGE,{"blendedFrom":[makeQuery(id+"F1.opExtrude","CAP_EDGE",EDGE,{"disambiguationData":[OSD([subQ0])],"isStart":true}),makeQuery(id+"F1.opExtrude","CAP_FACE",FACE,{"disambiguationData":[OSD([sQuery(id+"F0.wireOp",EDGE,"E0.0"),subQ0,sQuery(id+"F0.wireOp",EDGE,"E0.2"),sQuery(id+"F0.wireOp",EDGE,"E0.3"),sQuery(id+"F0.wireOp",EDGE,"E0.4"),sQuery(id+"F0.wireOp",EDGE,"E0.5"),sQuery(id+"F0.wireOp",EDGE,"E0.6"),sQuery(id+"F0.wireOp",EDGE,"E0.7"),sQuery(id+"F0.wireOp",EDGE,"E0.8"),sQuery(id+"F0.wireOp",EDGE,"E0.9"),sQuery(id+"F0.wireOp",EDGE,"E0.10"),sQuery(id+"F0.wireOp",EDGE,"E0.11"),sQuery(id+"F0.wireOp",EDGE,"E0.12"),sQuery(id+"F0.wireOp",EDGE,"E0.13"),sQuery(id+"F0.wireOp",EDGE,"E0.14"),sQuery(id+"F0.wireOp",EDGE,"E0.15")])],"isStart":true})],"blendedInto":[makeQuery(id+"F1.opExtrude","CAP_FACE",FACE,{"disambiguationData":[OSD([sQuery(id+"F0.wireOp",EDGE,"E0.0"),subQ0,sQuery(id+"F0.wireOp",EDGE,"E0.2"),sQuery(id+"F0.wireOp",EDGE,"E0.3"),sQuery(id+"F0.wireOp",EDGE,"E0.4"),sQuery(id+"F0.wireOp",EDGE,"E0.5"),sQuery(id+"F0.wireOp",EDGE,"E0.6"),sQuery(id+"F0.wireOp",EDGE,"E0.7"),sQuery(id+"F0.wireOp",EDGE,"E0.8"),sQuery(id+"F0.wireOp",EDGE,"E0.9"),sQuery(id+"F0.wireOp",EDGE,"E0.10"),sQuery(id+"F0.wireOp",EDGE,"E0.11"),sQuery(id+"F0.wireOp",EDGE,"E0.12"),sQuery(id+"F0.wireOp",EDGE,"E0.13"),sQuery(id+"F0.wireOp",EDGE,"E0.14"),sQuery(id+"F0.wireOp",EDGE,"E0.15")])],"isStart":true})]});}
            chamfer(context, id + "F6", {"entities" : qUnion([Q0, Q1, Q2, Q3, Q4, Q5, Q6, Q7]), "width" : 7.62 * mm, "tangentPropagation" : true});
        }
    });
